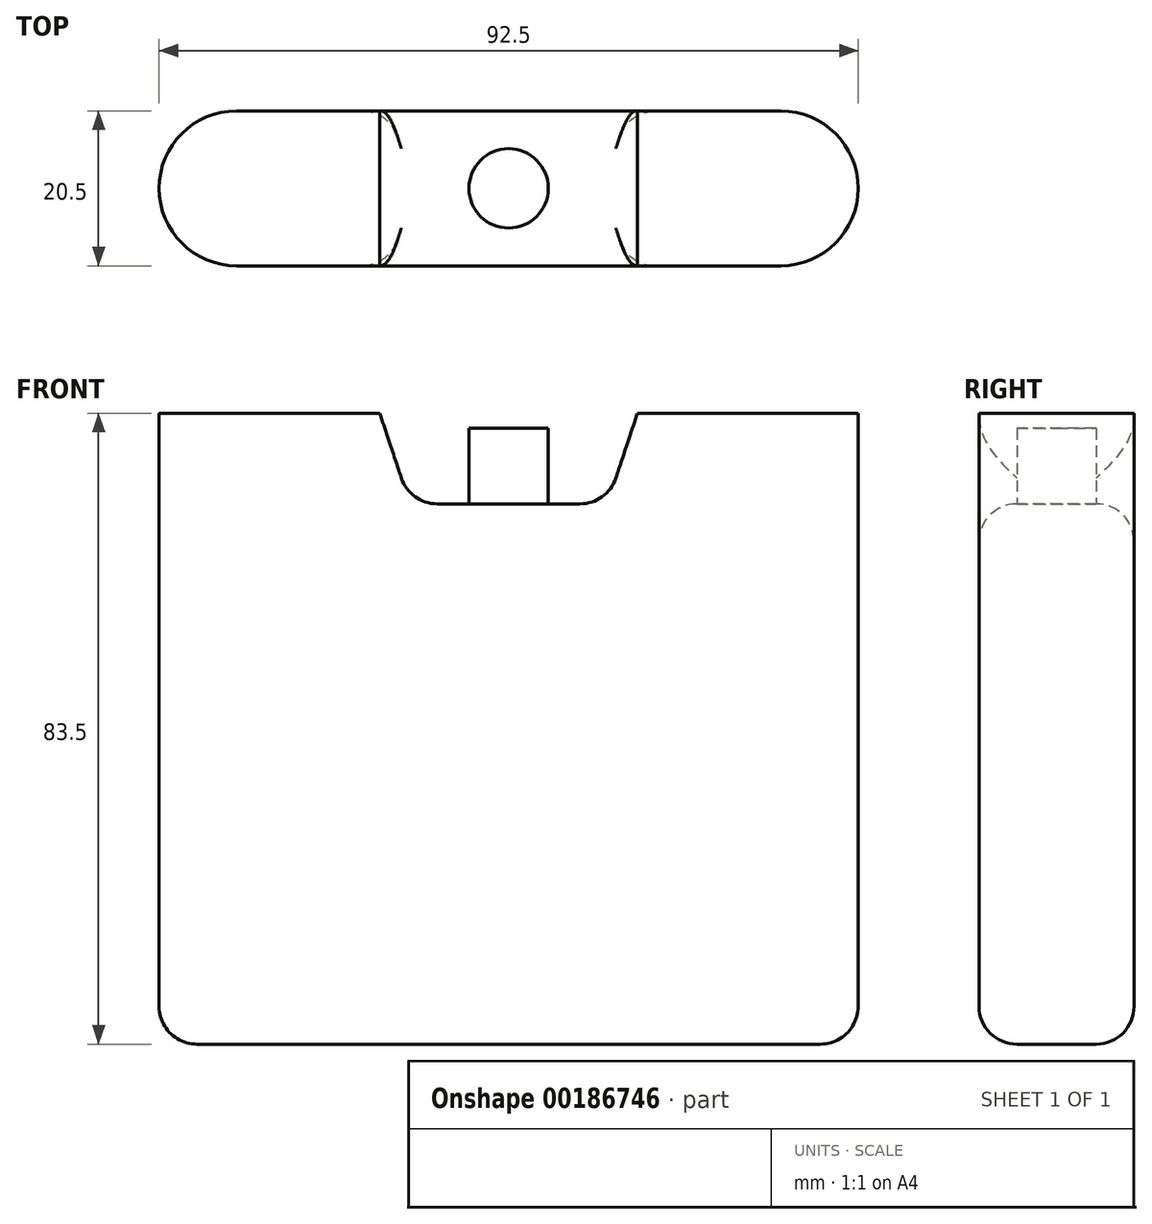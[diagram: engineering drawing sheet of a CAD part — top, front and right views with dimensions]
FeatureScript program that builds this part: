
annotation { "Feature Type Name" : "Feature", "Feature Type Description" : "" }
export const myFeature = defineFeature(function(context is Context, id is Id, definition is map)
    precondition{}
    {
        {
            var Q0;
            Q0=qCreatedBy(makeId("Front.planeOp"),FACE);
            var sketch = newSketch(context, id + "F0", { "sketchPlane" : qUnion([Q0])});
            skLineSegment(sketch, "E0", {"start": v(0, 0) * mm, "end": v(92.5, 0) * mm});
            skLineSegment(sketch, "E1", {"start": v(92.5, 0) * mm, "end": v(92.5, 83.5) * mm});
            skLineSegment(sketch, "E2", {"start": v(92.5, 83.5) * mm, "end": v(0, 83.5) * mm});
            skLineSegment(sketch, "E3", {"start": v(0, 83.5) * mm, "end": v(0, 0) * mm});
            skLineSegment(sketch, "E4", {"start": v(92.5, 83.5) * mm, "end": v(59.3, 83.5) * mm});
            skLineSegment(sketch, "E5", {"start": v(0, 83.5) * mm, "end": v(33.2, 83.5) * mm});
            skLineSegment(sketch, "E6", {"start": v(46.25, 0) * mm, "end": v(46.25, 71.5) * mm});
            skLineSegment(sketch, "E7", {"start": v(33.2, 71.5) * mm, "end": v(59.3, 71.5) * mm});
            skLineSegment(sketch, "E8", {"start": v(59.3, 71.5) * mm, "end": v(59.3, 83.5) * mm});
            skLineSegment(sketch, "E9", {"start": v(33.2, 83.5) * mm, "end": v(33.2, 71.5) * mm});
            skLineSegment(sketch, "E10", {"start": v(33.2, 71.5) * mm, "end": v(29.2, 83.5) * mm});
            skLineSegment(sketch, "E11", {"start": v(59.3, 71.5) * mm, "end": v(63.3, 83.5) * mm});
            skSolve(sketch);
        }
        {
            var Q0;
            {var subQ1=sQuery(id+"F0.wireOp",EDGE,"E3");Q0=makeQuery(id+"F0.imprint","IMPRINT",FACE,{"disambiguationData":[TD([[makeQuery(id+"F0.imprint","IMPRINT",EDGE,{"derivedFrom":subQ1}),1.0]])]});}
            var Q1;
            {var subQ1=sQuery(id+"F0.wireOp",EDGE,"E1");Q1=makeQuery(id+"F0.imprint","IMPRINT",FACE,{"disambiguationData":[TD([[makeQuery(id+"F0.imprint","IMPRINT",EDGE,{"derivedFrom":subQ1}),1.0]])]});}
            extrude(context, id + "F1", {"entities" : qUnion([Q0, Q1]), "depth" : 20.5 * mm});
        }
        {
            var Q0;
            Q0=makeQuery(id+"F1.opExtrude","CAP_EDGE",EDGE,{"disambiguationData":[OSD([sQuery(id+"F0.wireOp",EDGE,"E3")])],"isStart":false});
            var Q1;
            Q1=makeQuery(id+"F1.opExtrude","CAP_EDGE",EDGE,{"disambiguationData":[OSD([sQuery(id+"F0.wireOp",EDGE,"E3")])],"isStart":true});
            var Q2;
            Q2=makeQuery(id+"F1.opExtrude","CAP_EDGE",EDGE,{"disambiguationData":[OSD([sQuery(id+"F0.wireOp",EDGE,"E1")])],"isStart":false});
            var Q3;
            Q3=makeQuery(id+"F1.opExtrude","CAP_EDGE",EDGE,{"disambiguationData":[OSD([sQuery(id+"F0.wireOp",EDGE,"E1")])],"isStart":true});
            fillet(context, id + "F2", {"entities" : qUnion([Q0, Q1, Q2, Q3]), "radius" : 10.25 * mm, "tangentPropagation" : true, "allowEdgeOverflow" : false});
        }
        {
            var Q0;
            Q0=makeQuery(id+"F1.opExtrude","SWEPT_FACE",FACE,{"disambiguationData":[OSD([sQuery(id+"F0.wireOp",EDGE,"E4")])]});
            var Q1;
            Q1=makeQuery(id+"F1.opExtrude","SWEPT_FACE",FACE,{"disambiguationData":[OSD([sQuery(id+"F0.wireOp",EDGE,"E5")])]});
            var Q2;
            Q2=makeQuery(id+"F1.opExtrude","SWEPT_FACE",FACE,{"disambiguationData":[OSD([sQuery(id+"F0.wireOp",EDGE,"E0")])]});
            var Q3;
            Q3=makeQuery(id+"F1.opExtrude","SWEPT_FACE",FACE,{"disambiguationData":[OSD([sQuery(id+"F0.wireOp",EDGE,"E7")])]});
            fillet(context, id + "F3", {"entities" : qUnion([Q0, Q1, Q2, Q3]), "radius" : 5 * mm, "tangentPropagation" : true, "allowEdgeOverflow" : false});
        }
        {
            var Q0;
            Q0=makeQuery(id+"F1.opExtrude","SWEPT_FACE",FACE,{"disambiguationData":[OSD([sQuery(id+"F0.wireOp",EDGE,"E7")])]});
            var sketch = newSketch(context, id + "F4", { "sketchPlane" : qUnion([Q0])});
            skCircle(sketch, "E12", {"center": v(46.25, -10.25) * mm, "radius": 5.25 * mm});
            skPoint(sketch, "E12.centerSnap0", {"position": v(36.8, -10.25) * mm});
            skPoint(sketch, "E12.centerSnap1", {"position": v(46.25, -5) * mm});
            skSolve(sketch);
        }
        {
            var Q0;
            {var subQ0=sQuery(id+"F4.wireOp",EDGE,"E12");var subQ1=sQuery(id+"F0.wireOp",EDGE,"E7");var subQ2=makeQuery(id+"F1.opExtrude","SWEPT_FACE",FACE,{"disambiguationData":[OSD([subQ1])]});var subQ3=makeQuery(id+"F4.imprint","INTERSECT",VERTEX,{"derivedFrom":[makeQuery(id+"F3.opFillet","BLEND_EDGE",EDGE,{"blendedFrom":[makeQuery(id+"F1.opExtrude","CAP_EDGE",EDGE,{"disambiguationData":[OSD([subQ1])],"isStart":true}),subQ2],"blendedInto":[subQ2]}),subQ0]});Q0=makeQuery(id+"F4.imprint","IMPRINT",FACE,{"disambiguationData":[TD([[makeQuery(id+"F4.imprint","IMPRINT",EDGE,{"disambiguationData":[TD([[subQ3,-1.0]])],"derivedFrom":subQ0}),1.0]])]});}
            extrude(context, id + "F5", {"entities" : qUnion([Q0]), "operationType" : NewBodyOperationType.ADD, "depth" : 10 * mm});
        }
    });
